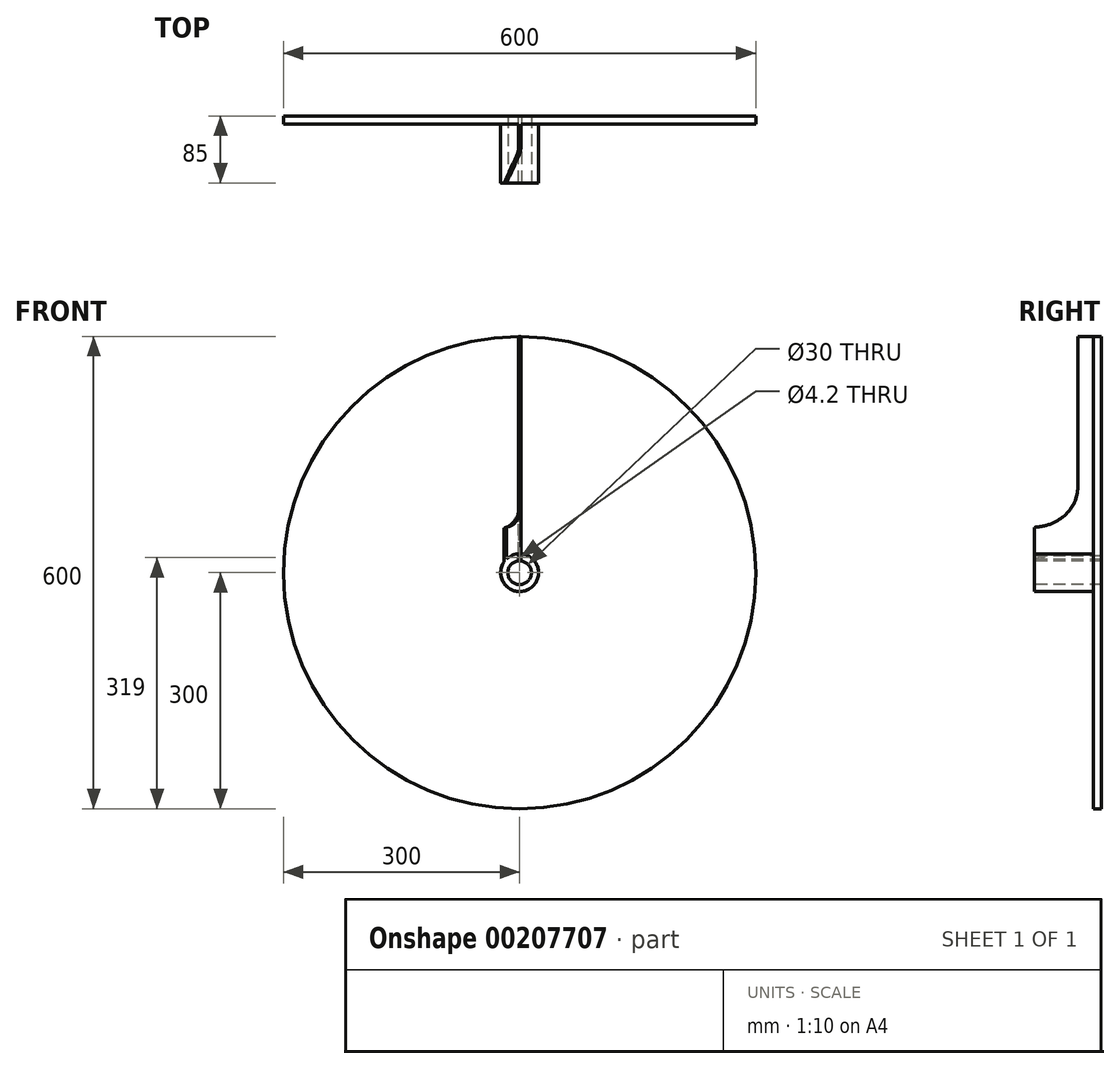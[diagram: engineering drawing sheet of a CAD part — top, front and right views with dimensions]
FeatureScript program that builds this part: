
annotation { "Feature Type Name" : "Feature", "Feature Type Description" : "" }
export const myFeature = defineFeature(function(context is Context, id is Id, definition is map)
    precondition{}
    {
        {
            var Q0;
            Q0=qCreatedBy(makeId("Front.planeOp"),FACE);
            var sketch = newSketch(context, id + "F0", { "sketchPlane" : qUnion([Q0])});
            skCircle(sketch, "E0", {"center": v(0, 0) * mm, "radius": 300 * mm});
            skSolve(sketch);
        }
        {
            var Q0;
            Q0 = qSketchRegion(id + "F0", true);
            extrude(context, id + "F1", {"entities" : qUnion([Q0]), "depth" : 10 * mm});
        }
        {
            var Q0;
            Q0=makeQuery(id+"F1.opExtrude","CAP_FACE",FACE,{"disambiguationData":[OSD([sQuery(id+"F0.wireOp",EDGE,"E0")])],"isStart":false});
            var sketch = newSketch(context, id + "F2", { "sketchPlane" : qUnion([Q0])});
            skCircle(sketch, "E1", {"center": v(0, 0) * mm, "radius": 24 * mm});
            skSolve(sketch);
        }
        {
            var Q0;
            Q0=makeQuery(id+"F2.imprint","IMPRINT",FACE,{"disambiguationData":[TD([[makeQuery(id+"F2.imprint","IMPRINT",EDGE,{"derivedFrom":sQuery(id+"F2.wireOp",EDGE,"E1")}),1.0]])]});
            extrude(context, id + "F3", {"entities" : qUnion([Q0]), "operationType" : NewBodyOperationType.ADD, "depth" : 75 * mm});
        }
        {
            var Q0;
            Q0=qCreatedBy(makeId("Top.planeOp"),FACE);
            var sketch = newSketch(context, id + "F4", { "sketchPlane" : qUnion([Q0])});
            skLineSegment(sketch, "E2.bottom", {"start": v(-1.5, 0) * mm, "end": v(1.5, 0) * mm});
            skLineSegment(sketch, "E2.top", {"start": v(-1.5, -45) * mm, "end": v(1.5, -45) * mm, "construction": true});
            skLineSegment(sketch, "E2.left", {"start": v(1.5, 0) * mm, "end": v(1.5, -40.66) * mm});
            skLineSegment(sketch, "E2.right", {"start": v(-1.5, 0) * mm, "end": v(-1.5, -40.66) * mm});
            skLineSegment(sketch, "E3", {"start": v(0, -45) * mm, "end": v(-18.23, -85) * mm, "construction": true});
            skLineSegment(sketch, "E4", {"start": v(-0.3, -48.95) * mm, "end": v(-16.73, -85) * mm});
            skLineSegment(sketch, "E5", {"start": v(-3.3, -48.95) * mm, "end": v(-19.73, -85) * mm});
            skPoint(sketch, "E6.visualSharp", {"position": v(-1.5, -45) * mm});
            skArc(sketch, "E6.filletArc", {"start": v(-3.3, -48.95) * mm, "mid": v(-1.96, -44.9) * mm, "end": v(-1.5, -40.66) * mm});
            skPoint(sketch, "E7.visualSharp", {"position": v(1.5, -45) * mm});
            skArc(sketch, "E7.filletArc", {"start": v(-0.3, -48.95) * mm, "mid": v(1.04, -44.9) * mm, "end": v(1.5, -40.66) * mm});
            skLineSegment(sketch, "E8", {"start": v(-19.73, -85) * mm, "end": v(-16.73, -85) * mm});
            skSolve(sketch);
        }
        {
            var Q0;
            Q0=qCreatedBy(makeId("Front.planeOp"),FACE);
            var sketch = newSketch(context, id + "F5", { "sketchPlane" : qUnion([Q0])});
            skLineSegment(sketch, "E9", {"start": v(0, 300) * mm, "end": v(0, 0) * mm, "construction": true});
            skSolve(sketch);
        }
        {
            var Q0;
            Q0 = qSketchRegion(id + "F4", true);
            var Q1;
            Q1=sQuery(id+"F5.wireOp",EDGE,"E9");
            var Q2;
            Q2 = qConstructionFilter(qBodyType(qCreatedBy(id + "F4" ,EDGE), BodyType.WIRE), ConstructionObject.NO);
            extrude(context, id + "F6", {"entities" : qUnion([Q0]), "operationType" : NewBodyOperationType.ADD, "surfaceEntities" : qUnion([Q1, Q2]), "depth" : 301 * mm});
        }
        {
            var Q0;
            Q0=qCreatedBy(makeId("Right.planeOp"),FACE);
            var sketch = newSketch(context, id + "F7", { "sketchPlane" : qUnion([Q0])});
            skLineSegment(sketch, "E10.bottom", {"start": v(-130, 360) * mm, "end": v(-30, 360) * mm});
            skLineSegment(sketch, "E10.top", {"start": v(-130, 60) * mm, "end": v(-80, 60) * mm});
            skLineSegment(sketch, "E10.left", {"start": v(-130, 360) * mm, "end": v(-130, 60) * mm});
            skLineSegment(sketch, "E10.right", {"start": v(-30, 360) * mm, "end": v(-30, 110) * mm});
            skPoint(sketch, "E11.visualSharp", {"position": v(-30, 60) * mm});
            skArc(sketch, "E11.filletArc", {"start": v(-80, 60) * mm, "mid": v(-44.64, 74.64) * mm, "end": v(-30, 110) * mm});
            skLineSegment(sketch, "E12.bottom", {"start": v(0, 360) * mm, "end": v(-30, 360) * mm});
            skLineSegment(sketch, "E12.top", {"start": v(0, 300) * mm, "end": v(-30, 300) * mm});
            skLineSegment(sketch, "E12.left", {"start": v(0, 360) * mm, "end": v(0, 300) * mm});
            skLineSegment(sketch, "E12.right", {"start": v(-30, 360) * mm, "end": v(-30, 300) * mm});
            skSolve(sketch);
        }
        {
            var Q0;
            Q0=makeQuery(id+"F7.imprint","IMPRINT",FACE,{"disambiguationData":[TD([[makeQuery(id+"F7.imprint","IMPRINT",EDGE,{"derivedFrom":sQuery(id+"F7.wireOp",EDGE,"E10.bottom")}),-1.0]])]});
            var Q1;
            Q1=makeQuery(id+"F7.imprint","IMPRINT",FACE,{"disambiguationData":[TD([[makeQuery(id+"F7.imprint","IMPRINT",EDGE,{"derivedFrom":sQuery(id+"F7.wireOp",EDGE,"E12.bottom")}),1.0]])]});
            var Q2;
            {var subQ1=sQuery(id+"F0.wireOp",EDGE,"E0");Q2=makeQuery(id+"FOiUgelMLmqVwCS_1.1.F6.boolean.opBoolean","SPLIT",FACE,{"disambiguationData":[TD([makeQuery(id+"F6.opExtrude","SWEPT_FACE",FACE,{"disambiguationData":[OSD([sQuery(id+"F4.wireOp",EDGE,"E2.left")])]})])],"derivedFrom":makeQuery(id+"F1.opExtrude","SWEPT_FACE",FACE,{"disambiguationData":[OSD([subQ1])]})});}
            revolve(context, id + "F8", {"operationType" : NewBodyOperationType.REMOVE, "entities" : qUnion([Q0, Q1]), "axis" : qUnion([Q2]), "revolveType" : RevolveType.FULL, "oppositeDirection" : true});
        }
        {
            var Q0;
            {var subQ0=sQuery(id+"F4.wireOp",EDGE,"E8");Q0=makeQuery(id+"FOiUgelMLmqVwCS_1.19.F6.boolean.opBoolean","MERGE",FACE,{"derivedFrom":[makeQuery(id+"FOiUgelMLmqVwCS_1.18.F6.boolean.opBoolean","MERGE",FACE,{"derivedFrom":[makeQuery(id+"FOiUgelMLmqVwCS_1.17.F6.boolean.opBoolean","MERGE",FACE,{"derivedFrom":[makeQuery(id+"FOiUgelMLmqVwCS_1.16.F6.boolean.opBoolean","MERGE",FACE,{"derivedFrom":[makeQuery(id+"FOiUgelMLmqVwCS_1.15.F6.boolean.opBoolean","MERGE",FACE,{"derivedFrom":[makeQuery(id+"FOiUgelMLmqVwCS_1.14.F6.boolean.opBoolean","MERGE",FACE,{"derivedFrom":[makeQuery(id+"FOiUgelMLmqVwCS_1.13.F6.boolean.opBoolean","MERGE",FACE,{"derivedFrom":[makeQuery(id+"FOiUgelMLmqVwCS_1.12.F6.boolean.opBoolean","MERGE",FACE,{"derivedFrom":[makeQuery(id+"FOiUgelMLmqVwCS_1.11.F6.boolean.opBoolean","MERGE",FACE,{"derivedFrom":[makeQuery(id+"FOiUgelMLmqVwCS_1.10.F6.boolean.opBoolean","MERGE",FACE,{"derivedFrom":[makeQuery(id+"FOiUgelMLmqVwCS_1.9.F6.boolean.opBoolean","MERGE",FACE,{"derivedFrom":[makeQuery(id+"FOiUgelMLmqVwCS_1.8.F6.boolean.opBoolean","MERGE",FACE,{"derivedFrom":[makeQuery(id+"FOiUgelMLmqVwCS_1.7.F6.boolean.opBoolean","MERGE",FACE,{"derivedFrom":[makeQuery(id+"FOiUgelMLmqVwCS_1.6.F6.boolean.opBoolean","MERGE",FACE,{"derivedFrom":[makeQuery(id+"FOiUgelMLmqVwCS_1.5.F6.boolean.opBoolean","MERGE",FACE,{"derivedFrom":[makeQuery(id+"FOiUgelMLmqVwCS_1.4.F6.boolean.opBoolean","MERGE",FACE,{"derivedFrom":[makeQuery(id+"FOiUgelMLmqVwCS_1.3.F6.boolean.opBoolean","MERGE",FACE,{"derivedFrom":[makeQuery(id+"FOiUgelMLmqVwCS_1.2.F6.boolean.opBoolean","MERGE",FACE,{"derivedFrom":[makeQuery(id+"FOiUgelMLmqVwCS_1.1.F6.boolean.opBoolean","MERGE",FACE,{"derivedFrom":[makeQuery(id+"F6.boolean.opBoolean","MERGE",FACE,{"derivedFrom":[makeQuery(id+"F3.opExtrude","CAP_FACE",FACE,{"disambiguationData":[OSD([sQuery(id+"F2.wireOp",EDGE,"E1")])],"isStart":false}),makeQuery(id+"F6.opExtrude","SWEPT_FACE",FACE,{"disambiguationData":[OSD([subQ0])]})]}),makeQuery(id+"FOiUgelMLmqVwCS_1.1.F6.opExtrude","SWEPT_FACE",FACE,{"disambiguationData":[OSD([subQ0])]})]}),makeQuery(id+"FOiUgelMLmqVwCS_1.2.F6.opExtrude","SWEPT_FACE",FACE,{"disambiguationData":[OSD([subQ0])]})]}),makeQuery(id+"FOiUgelMLmqVwCS_1.3.F6.opExtrude","SWEPT_FACE",FACE,{"disambiguationData":[OSD([subQ0])]})]}),makeQuery(id+"FOiUgelMLmqVwCS_1.4.F6.opExtrude","SWEPT_FACE",FACE,{"disambiguationData":[OSD([subQ0])]})]}),makeQuery(id+"FOiUgelMLmqVwCS_1.5.F6.opExtrude","SWEPT_FACE",FACE,{"disambiguationData":[OSD([subQ0])]})]}),makeQuery(id+"FOiUgelMLmqVwCS_1.6.F6.opExtrude","SWEPT_FACE",FACE,{"disambiguationData":[OSD([subQ0])]})]}),makeQuery(id+"FOiUgelMLmqVwCS_1.7.F6.opExtrude","SWEPT_FACE",FACE,{"disambiguationData":[OSD([subQ0])]})]}),makeQuery(id+"FOiUgelMLmqVwCS_1.8.F6.opExtrude","SWEPT_FACE",FACE,{"disambiguationData":[OSD([subQ0])]})]}),makeQuery(id+"FOiUgelMLmqVwCS_1.9.F6.opExtrude","SWEPT_FACE",FACE,{"disambiguationData":[OSD([subQ0])]})]}),makeQuery(id+"FOiUgelMLmqVwCS_1.10.F6.opExtrude","SWEPT_FACE",FACE,{"disambiguationData":[OSD([subQ0])]})]}),makeQuery(id+"FOiUgelMLmqVwCS_1.11.F6.opExtrude","SWEPT_FACE",FACE,{"disambiguationData":[OSD([subQ0])]})]}),makeQuery(id+"FOiUgelMLmqVwCS_1.12.F6.opExtrude","SWEPT_FACE",FACE,{"disambiguationData":[OSD([subQ0])]})]}),makeQuery(id+"FOiUgelMLmqVwCS_1.13.F6.opExtrude","SWEPT_FACE",FACE,{"disambiguationData":[OSD([subQ0])]})]}),makeQuery(id+"FOiUgelMLmqVwCS_1.14.F6.opExtrude","SWEPT_FACE",FACE,{"disambiguationData":[OSD([subQ0])]})]}),makeQuery(id+"FOiUgelMLmqVwCS_1.15.F6.opExtrude","SWEPT_FACE",FACE,{"disambiguationData":[OSD([subQ0])]})]}),makeQuery(id+"FOiUgelMLmqVwCS_1.16.F6.opExtrude","SWEPT_FACE",FACE,{"disambiguationData":[OSD([subQ0])]})]}),makeQuery(id+"FOiUgelMLmqVwCS_1.17.F6.opExtrude","SWEPT_FACE",FACE,{"disambiguationData":[OSD([subQ0])]})]}),makeQuery(id+"FOiUgelMLmqVwCS_1.18.F6.opExtrude","SWEPT_FACE",FACE,{"disambiguationData":[OSD([subQ0])]})]}),makeQuery(id+"FOiUgelMLmqVwCS_1.19.F6.opExtrude","SWEPT_FACE",FACE,{"disambiguationData":[OSD([subQ0])]})]});}
            var sketch = newSketch(context, id + "F9", { "sketchPlane" : qUnion([Q0])});
            skCircle(sketch, "E13", {"center": v(0, 0) * mm, "radius": 15 * mm});
            skSolve(sketch);
        }
        {
            var Q0;
            Q0 = qSketchRegion(id + "F9", true);
            extrude(context, id + "F10", {"entities" : qUnion([Q0]), "operationType" : NewBodyOperationType.REMOVE, "endBound" : BoundingType.UP_TO_NEXT, "oppositeDirection" : true, "depth" : 25 * mm});
        }
        {
            var Q0;
            {var subQ0=sQuery(id+"F4.wireOp",EDGE,"E8");Q0=makeQuery(id+"FOiUgelMLmqVwCS_1.19.F6.boolean.opBoolean","MERGE",FACE,{"derivedFrom":[makeQuery(id+"FOiUgelMLmqVwCS_1.18.F6.boolean.opBoolean","MERGE",FACE,{"derivedFrom":[makeQuery(id+"FOiUgelMLmqVwCS_1.17.F6.boolean.opBoolean","MERGE",FACE,{"derivedFrom":[makeQuery(id+"FOiUgelMLmqVwCS_1.16.F6.boolean.opBoolean","MERGE",FACE,{"derivedFrom":[makeQuery(id+"FOiUgelMLmqVwCS_1.15.F6.boolean.opBoolean","MERGE",FACE,{"derivedFrom":[makeQuery(id+"FOiUgelMLmqVwCS_1.14.F6.boolean.opBoolean","MERGE",FACE,{"derivedFrom":[makeQuery(id+"FOiUgelMLmqVwCS_1.13.F6.boolean.opBoolean","MERGE",FACE,{"derivedFrom":[makeQuery(id+"FOiUgelMLmqVwCS_1.12.F6.boolean.opBoolean","MERGE",FACE,{"derivedFrom":[makeQuery(id+"FOiUgelMLmqVwCS_1.11.F6.boolean.opBoolean","MERGE",FACE,{"derivedFrom":[makeQuery(id+"FOiUgelMLmqVwCS_1.10.F6.boolean.opBoolean","MERGE",FACE,{"derivedFrom":[makeQuery(id+"FOiUgelMLmqVwCS_1.9.F6.boolean.opBoolean","MERGE",FACE,{"derivedFrom":[makeQuery(id+"FOiUgelMLmqVwCS_1.8.F6.boolean.opBoolean","MERGE",FACE,{"derivedFrom":[makeQuery(id+"FOiUgelMLmqVwCS_1.7.F6.boolean.opBoolean","MERGE",FACE,{"derivedFrom":[makeQuery(id+"FOiUgelMLmqVwCS_1.6.F6.boolean.opBoolean","MERGE",FACE,{"derivedFrom":[makeQuery(id+"FOiUgelMLmqVwCS_1.5.F6.boolean.opBoolean","MERGE",FACE,{"derivedFrom":[makeQuery(id+"FOiUgelMLmqVwCS_1.4.F6.boolean.opBoolean","MERGE",FACE,{"derivedFrom":[makeQuery(id+"FOiUgelMLmqVwCS_1.3.F6.boolean.opBoolean","MERGE",FACE,{"derivedFrom":[makeQuery(id+"FOiUgelMLmqVwCS_1.2.F6.boolean.opBoolean","MERGE",FACE,{"derivedFrom":[makeQuery(id+"FOiUgelMLmqVwCS_1.1.F6.boolean.opBoolean","MERGE",FACE,{"derivedFrom":[makeQuery(id+"F6.boolean.opBoolean","MERGE",FACE,{"derivedFrom":[makeQuery(id+"F3.opExtrude","CAP_FACE",FACE,{"disambiguationData":[OSD([sQuery(id+"F2.wireOp",EDGE,"E1")])],"isStart":false}),makeQuery(id+"F6.opExtrude","SWEPT_FACE",FACE,{"disambiguationData":[OSD([subQ0])]})]}),makeQuery(id+"FOiUgelMLmqVwCS_1.1.F6.opExtrude","SWEPT_FACE",FACE,{"disambiguationData":[OSD([subQ0])]})]}),makeQuery(id+"FOiUgelMLmqVwCS_1.2.F6.opExtrude","SWEPT_FACE",FACE,{"disambiguationData":[OSD([subQ0])]})]}),makeQuery(id+"FOiUgelMLmqVwCS_1.3.F6.opExtrude","SWEPT_FACE",FACE,{"disambiguationData":[OSD([subQ0])]})]}),makeQuery(id+"FOiUgelMLmqVwCS_1.4.F6.opExtrude","SWEPT_FACE",FACE,{"disambiguationData":[OSD([subQ0])]})]}),makeQuery(id+"FOiUgelMLmqVwCS_1.5.F6.opExtrude","SWEPT_FACE",FACE,{"disambiguationData":[OSD([subQ0])]})]}),makeQuery(id+"FOiUgelMLmqVwCS_1.6.F6.opExtrude","SWEPT_FACE",FACE,{"disambiguationData":[OSD([subQ0])]})]}),makeQuery(id+"FOiUgelMLmqVwCS_1.7.F6.opExtrude","SWEPT_FACE",FACE,{"disambiguationData":[OSD([subQ0])]})]}),makeQuery(id+"FOiUgelMLmqVwCS_1.8.F6.opExtrude","SWEPT_FACE",FACE,{"disambiguationData":[OSD([subQ0])]})]}),makeQuery(id+"FOiUgelMLmqVwCS_1.9.F6.opExtrude","SWEPT_FACE",FACE,{"disambiguationData":[OSD([subQ0])]})]}),makeQuery(id+"FOiUgelMLmqVwCS_1.10.F6.opExtrude","SWEPT_FACE",FACE,{"disambiguationData":[OSD([subQ0])]})]}),makeQuery(id+"FOiUgelMLmqVwCS_1.11.F6.opExtrude","SWEPT_FACE",FACE,{"disambiguationData":[OSD([subQ0])]})]}),makeQuery(id+"FOiUgelMLmqVwCS_1.12.F6.opExtrude","SWEPT_FACE",FACE,{"disambiguationData":[OSD([subQ0])]})]}),makeQuery(id+"FOiUgelMLmqVwCS_1.13.F6.opExtrude","SWEPT_FACE",FACE,{"disambiguationData":[OSD([subQ0])]})]}),makeQuery(id+"FOiUgelMLmqVwCS_1.14.F6.opExtrude","SWEPT_FACE",FACE,{"disambiguationData":[OSD([subQ0])]})]}),makeQuery(id+"FOiUgelMLmqVwCS_1.15.F6.opExtrude","SWEPT_FACE",FACE,{"disambiguationData":[OSD([subQ0])]})]}),makeQuery(id+"FOiUgelMLmqVwCS_1.16.F6.opExtrude","SWEPT_FACE",FACE,{"disambiguationData":[OSD([subQ0])]})]}),makeQuery(id+"FOiUgelMLmqVwCS_1.17.F6.opExtrude","SWEPT_FACE",FACE,{"disambiguationData":[OSD([subQ0])]})]}),makeQuery(id+"FOiUgelMLmqVwCS_1.18.F6.opExtrude","SWEPT_FACE",FACE,{"disambiguationData":[OSD([subQ0])]})]}),makeQuery(id+"FOiUgelMLmqVwCS_1.19.F6.opExtrude","SWEPT_FACE",FACE,{"disambiguationData":[OSD([subQ0])]})]});}
            var sketch = newSketch(context, id + "F11", { "sketchPlane" : qUnion([Q0])});
            skCircle(sketch, "E14", {"center": v(0, 19) * mm, "radius": 2.5 * mm});
            skSolve(sketch);
        }
        {
            var Q0;
            Q0=sQuery(id+"F11.wireOp",VERTEX,"E14.center");
            var Q1;
            Q1=makeQuery(id+"F1.opExtrude","SWEPT_BODY",BODY,{"disambiguationData":[OSD([sQuery(id+"F0.wireOp",EDGE,"E0")])]});
            hole(context, id + "F12", {"style" : HoleStyle.SIMPLE, "endStyle" : HoleEndStyle.THROUGH, "standardTappedOrClearance" : lookupTablePath({ "standard" : "ISO", "engagement" : "75%", "pitch" : "0.8 mm", "size" : "M5", "type" : "Tapped" }), "standardBlindInLast" : lookupTablePath({ "standard" : "ISO", "engagement" : "75%", "pitch" : "0.8 mm", "size" : "M5", "type" : "Tapped" }), "holeDiameter" : 4.2 * mm, "showTappedDepth" : true, "tappedDepth" : 12 * mm, "tapClearance" : 3, "locations" : qUnion([Q0]), "scope" : qUnion([Q1]), "majorDiameter" : 5 * mm});
        }
    });
